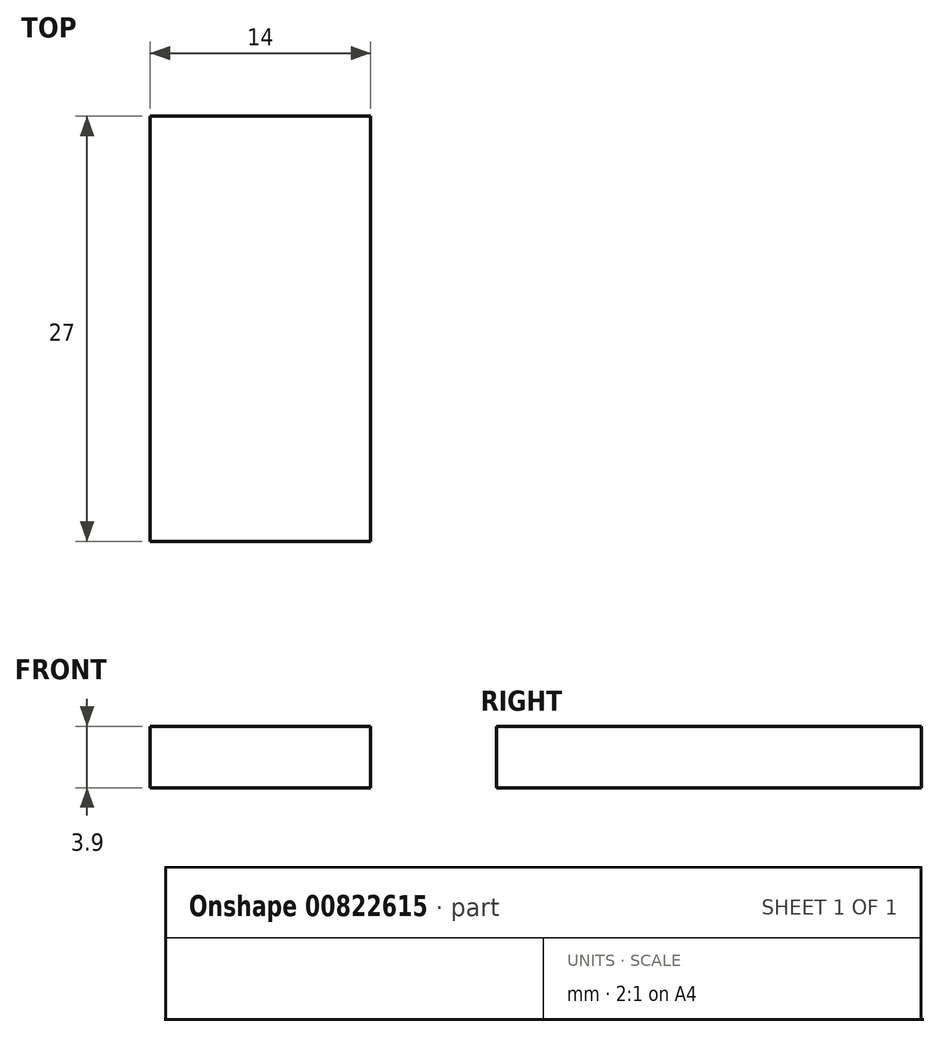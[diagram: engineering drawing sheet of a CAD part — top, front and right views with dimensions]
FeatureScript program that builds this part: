
annotation { "Feature Type Name" : "Feature", "Feature Type Description" : "" }
export const myFeature = defineFeature(function(context is Context, id is Id, definition is map)
    precondition{}
    {
        {
            var Q0;
            Q0=qCreatedBy(makeId("Top.planeOp"),FACE);
            var sketch = newSketch(context, id + "F0", { "sketchPlane" : qUnion([Q0])});
            skLineSegment(sketch, "E0.bottom", {"start": v(7, -13.5) * mm, "end": v(-7, -13.5) * mm});
            skLineSegment(sketch, "E0.top", {"start": v(7, 13.5) * mm, "end": v(-7, 13.5) * mm});
            skLineSegment(sketch, "E0.left", {"start": v(7, -13.5) * mm, "end": v(7, 13.5) * mm});
            skLineSegment(sketch, "E0.right", {"start": v(-7, -13.5) * mm, "end": v(-7, 13.5) * mm});
            skPoint(sketch, "E0.middle", {"position": v(0, 0) * mm});
            skSolve(sketch);
        }
        {
            var Q0;
            Q0 = qSketchRegion(id + "F0", true);
            extrude(context, id + "F1", {"entities" : qUnion([Q0]), "depth" : 3.9 * mm, "offsetDistance" : 25 * mm});
        }
    });
